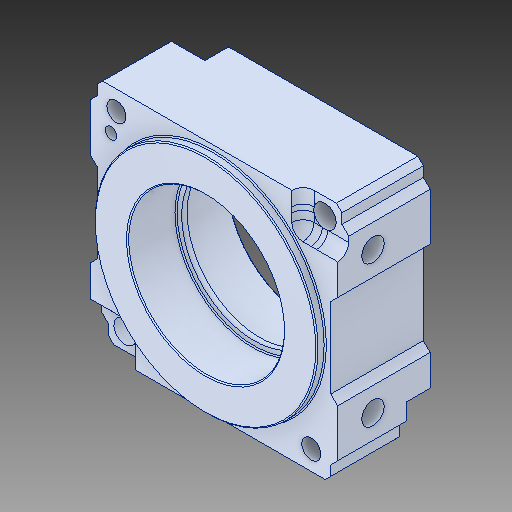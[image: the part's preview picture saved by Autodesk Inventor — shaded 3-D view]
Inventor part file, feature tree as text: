
AUTODESK INVENTOR PART (.ipt)
format: ipt  version: 2017 (Build 210142000, 142)  size: 249,856 bytes
history: native  units: in
note: dims shown in document units (in); Inventor stores cm internally (conversion verified against a paired STEP export)
features: chamfer x1
ambient origin geometry x8: Origin, YZ Plane, XZ Plane, XY Plane, X Axis, Y Axis, Z Axis, Center Point
bodies: Solid1 (feature_tree)
feature tree (1):
  chamfer  "Chamfer2"  [1 undecoded]
note: 1 required parameter value undecoded (feature->parameter linkage not recoverable at this tier; creation-order binding heuristic only, values carry confidence <= 0.55)
